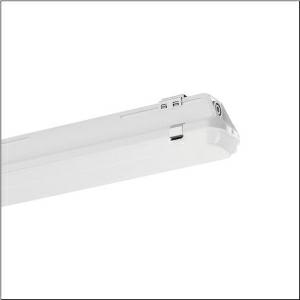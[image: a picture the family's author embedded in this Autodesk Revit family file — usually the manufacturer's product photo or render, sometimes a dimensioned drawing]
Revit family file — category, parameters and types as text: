
# Revit family: monsun_11_51fp10fp460l
name_source: partatom
category: Lighting Fixtures
units: mm (PartAtom-declared; Revit-internal decimal feet)

## family parameters
Cut with Voids When Loaded = No
Host = Face
Light Source = No
Part Type = Normal
Room Calculation Point = No
Round Connector Dimension = Use Diameter
Shared = No

## types (1)
- --- (1 x LED, 6050 lm, 31.5 W, 4000K)
    Apparent Load = 32 VA
    CIE Flux Codes = 47 77 93 94 100
    Color Rendering = 80
    Color Temperature = 4000K
    Default Elevation = 1800 mm
    Description = Monsun 11, damp-proof luminaire, chain hanger, primary optical cover: enclosure, of PMMA, light emission: direct distribution, primary light characteristic: symmetric, installation type: suspended mounting, surface-mounted, horizontal mounting, vertical mounting, LED, rated luminous flux: 6.050lm, luminous efficacy: 192lm/W, light colour: 840, colour temperature: 4000K, control gear: DALI 2, CLO, with terminal, 5-pole, max. 2.5mm², mains connection: 220..240V, AC, 50/60Hz, rated input power: 32W, luminaire housing, of glass-fibre reinforced polyester, uncoated, bright grey, incl. chain hanger, length: 1.590mm, width: 90mm, height: 88mm, clip for enclosure, of stainless steel (V2A), ceiling mounting element, of stainless steel (V2A), chain hanger, of stainless steel (V2A), protection rating (complete): IP66, insulation class (complete): insulation class I (protective earthing), certification: CE, ENEC, VDE, UKCA, protection symbol: D, impact resistance: IK04, permissible operating ambient temperature: -25..+35°C, standard: EN 50419, EN 60598-2-1, corresponds to IFS (International Featured Standards) requirements for safety and quality in the food industry, for indoor or canopied outdoor use, no direct snow, no direct sun, no direct rain, LABS conformity tested according to VDMA 24364:2018-05, contact your sales advisor before using the luminaires in applications with unclear chemical exposure, large temperature fluctuations or condensation-forming humidity, packaging unit: 1 piece
    Height = 89 mm
    Lamp = 1 x LED
    Lamp Light Flux = 6050 lm
    Lamp Power = 31.5 W
    Lamp count = 1
    Length = 1590 mm
    Luminous efficacy = 192 lm/W
    Manufacturer = Siteco
    ModVariant = No
    Model = 51FP10FP460L
    Mounting Place = Ceiling
    Mounting Type = Surface mounted
    Number of Poles = 1
    OnlyDefault = Yes
    Power Factor = 1
    Product Name = Monsun 11
    Product group = damp-proof luminaire
    ProductGroupID = 300
    Protection Class = Protection class I
    Protection Degree = IP 66
    RLX_Detail_Level = 1
    RLX_Emergency_Light_Flux = 0 lm
    RLX_Emergency_Type = 0
    RLX_Emergency_Type_DB = No
    RlxData = <blob elided: 92405 chars, md5=c057fb27>
    Socket = socket
    Standby Power = 0 W
    System Light Flux = 6050 lm
    System Power = 32 W
    Type Comments = factory setting: luminous flux: 100 % | dim-lin: 254 | 219 mA
    Type Image = l_1349237.jpg
    URL = http://relux.com
    VarID = @adj_033429
    Voltage = 0 V
    Weight = 0.00 kg
    Width = 90 mm

## geometry (parser evidence)
native form markers: Blend x4, Sweep x14
no freeform markers — native parametric forms only
